# Revit family: IS_TonicII_K8192_BIM_DE
name_source: partatom
category: Plumbing Fixtures
revit_build: Autodesk Revit MEP 2016 (Build: 20161004_0715(x64)
units: mm (PartAtom-declared; Revit-internal decimal feet)

## family parameters
Always vertical = No
Cut with Voids When Loaded = No
OmniClass Number = 23.45.05.14.21.11
OmniClass Title = Bath/Shower Units
Part Type = Normal
Room Calculation Point = No
Round Connector Dimension = Use Diameter
Shared = No
Work Plane-Based = No

## types (1)
- K819201 - panel for shower bath tub 2100x560mm
    Accessories = www.idealstandard.de\ersatzteile
    AreaUnits = millimeters
    AssetType = Fixed
    BIMObjectName = ISI_IdealStandard_Furniture_Tonic Ii_K819201
    BIMobject category = Screens & Dividers
    BOSUseNativeGeometries = 1
    BarCode = 4015413066709
    Brand = Ideal Standard
    Brand url = http://www.idealstandard.co.uk
    Color = White
    ConnectionType = Mechanical
    CurrencyUnit = €
    Date of publishing = 06/11/2017
    Description = K819201 panel for shower bath tub 2100x560mm
    DurationUnit = year
    EAN code = https://4015413066709
    Edition number = 1
    ExpectedLife = 25
    Features = panel for shower bath tub 2100x560mm
    Finish = White
    IFC Classification = Sanitary Terminal
    IfcExportAs = Sanitary Terminal Type
    IfcExportType = Baths
    Installation instructions = http://www.idealstandard.de
    InstallationInstructions = www.idealstandard.de\produkte
    LinearUnits = millimeters
    MainColor = White
    MaintenanceInformation = www.idealstandard.de\produkte
    Manufacturer name = Ideal Standard
    ManufacturerURL = www.idealstandard.com
    Material main = Acrylic
    Model = K819201
    ModelNumber = K819201
    ModelReference = panel for shower bath tub 2100x560mm
    NBS Reference Code = 35-06-08
    NBS Reference Description = Baths
    Name = Furniture_Tonic Ii_K819201_IdealStandard
    NettWeight = 6 kg
    Nominal height = 560
    Nominal width = 2000
    NominalDepth = 1506 mm  [stored 4.94094 ft]
    NominalHeight = 590 mm
    NominalLength = 1506 mm  [stored 4.94094 ft]
    NominalWidth = 1504 mm
    OmniClass Code = 23-31 15 00
    OmniClass Description = Bathtubs
    Product Guid = 04e9590c-19a6-4070-b1f9-08928cae927c
    Product SKU = K8192
    Product data url = https://bimobject.com
    Product family = TONIC II
    Product group = Bath Panel
    Product name = panel for shower bath tub 2100x560mm
    Product url = http://www.idealstandard.de
    ProductInformation = www.idealstandard.de/produkte
    QR code = http://bimobject.com
    Shape = Rectangular
    Size = 590 x 1506 x 1504mm
    Space = Internal
    SpareParts = www.idealstandard.de/ersatzteile
    Technical description = http://www.idealstandard.de
    URL = www.idealstandard.com
    Uniclass 1.4 Code = L7211
    Uniclass 1.4 Description = Baths
    Uniclass 2.0 Code = PR-35-06-08
    Uniclass 2.0 Description = Baths
    Uniclass 2015 Code = Pr_40_20_06_08
    Uniclass 2015 Name = Baths
    Uniclass2015Code = Pr_40_20_06_08
    Uniclass2015Title = Baths
    Uniclass2015Version = Products v1.1
    Version = 1
    VolumeUnits = Litres
    Weight Net (Kg) = 6

note: [stored X ft] marks values corroborated as IEEE doubles in the binary element streams (Revit-internal decimal feet)

## geometry (parser evidence)
native form markers: Blend x4
no freeform markers — native parametric forms only
